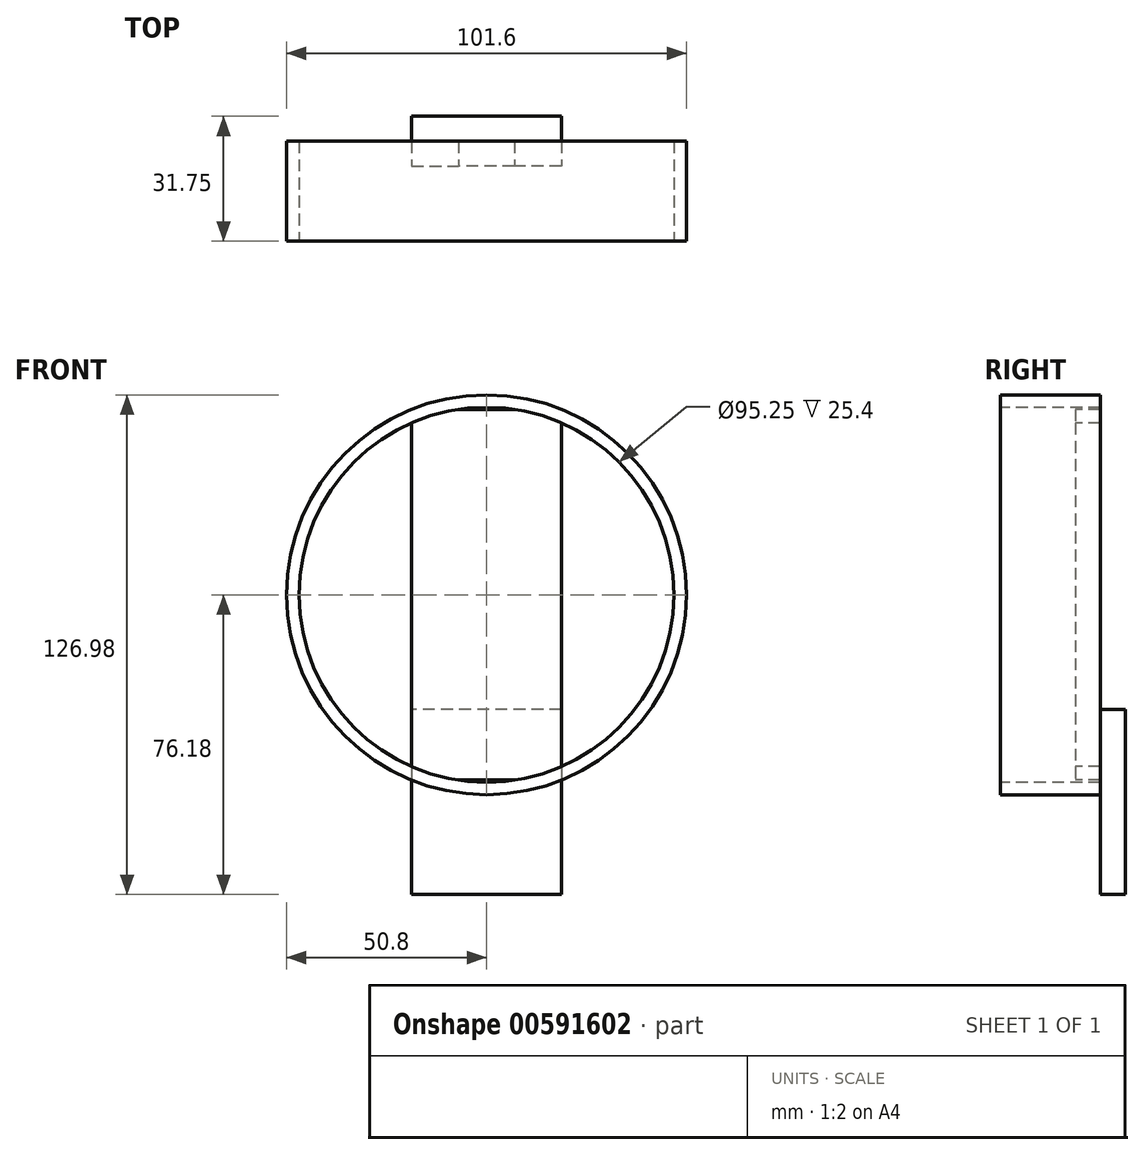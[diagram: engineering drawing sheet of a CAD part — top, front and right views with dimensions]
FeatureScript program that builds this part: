
annotation { "Feature Type Name" : "Feature", "Feature Type Description" : "" }
export const myFeature = defineFeature(function(context is Context, id is Id, definition is map)
    precondition{}
    {
        {
            var Q0;
            Q0=qCreatedBy(makeId("Front.planeOp"),FACE);
            var sketch = newSketch(context, id + "F0", { "sketchPlane" : qUnion([Q0])});
            skCircle(sketch, "E0", {"center": v(0, 0) * mm, "radius": 50.8 * mm});
            skSolve(sketch);
        }
        {
            var Q0;
            Q0 = qSketchRegion(id + "F0", true);
            extrude(context, id + "F1", {"entities" : qUnion([Q0]), "oppositeDirection" : true, "depth" : 25.4 * mm, "offsetDistance" : 25.4 * mm});
        }
        {
            var Q0;
            Q0=makeQuery(id+"F1.opExtrude","CAP_FACE",FACE,{"disambiguationData":[OSD([sQuery(id+"F0.wireOp",EDGE,"E0")])],"isStart":true});
            var sketch = newSketch(context, id + "F2", { "sketchPlane" : qUnion([Q0])});
            skCircle(sketch, "E1", {"center": v(0, 0) * mm, "radius": 47.63 * mm});
            skSolve(sketch);
        }
        {
            var Q0;
            Q0=makeQuery(id+"F2.imprint","IMPRINT",FACE,{"disambiguationData":[TD([[makeQuery(id+"F2.imprint","IMPRINT",EDGE,{"derivedFrom":sQuery(id+"F2.wireOp",EDGE,"E1")}),1.0]])]});
            extrude(context, id + "F3", {"entities" : qUnion([Q0]), "operationType" : NewBodyOperationType.REMOVE, "oppositeDirection" : true, "depth" : 25.4 * mm, "offsetDistance" : 25.4 * mm});
        }
        {
            var Q0;
            Q0=makeQuery(id+"F1.opExtrude","CAP_FACE",FACE,{"disambiguationData":[OSD([sQuery(id+"F0.wireOp",EDGE,"E0")])],"isStart":false});
            var sketch = newSketch(context, id + "F4", { "sketchPlane" : qUnion([Q0])});
            skLineSegment(sketch, "E2.bottom", {"start": v(-19.05, 47.1) * mm, "end": v(19.05, 47.1) * mm});
            skLineSegment(sketch, "E2.top", {"start": v(-19.05, -47.1) * mm, "end": v(19.05, -47.1) * mm});
            skLineSegment(sketch, "E2.left", {"start": v(-19.05, 47.1) * mm, "end": v(-19.05, -47.1) * mm});
            skLineSegment(sketch, "E2.right", {"start": v(19.05, 47.1) * mm, "end": v(19.05, -47.1) * mm});
            skSolve(sketch);
        }
        {
            var Q0;
            Q0 = qSketchRegion(id + "F4", true);
            extrude(context, id + "F5", {"entities" : qUnion([Q0]), "operationType" : NewBodyOperationType.ADD, "oppositeDirection" : true, "depth" : 6.35 * mm, "offsetDistance" : 25.4 * mm});
        }
        {
            var Q0;
            Q0=makeQuery(id+"F5.boolean.opBoolean","MERGE",FACE,{"derivedFrom":[makeQuery(id+"F1.opExtrude","CAP_FACE",FACE,{"disambiguationData":[OSD([sQuery(id+"F0.wireOp",EDGE,"E0")])],"isStart":false}),makeQuery(id+"F5.opExtrude","CAP_FACE",FACE,{"disambiguationData":[OSD([sQuery(id+"F4.wireOp",EDGE,"E2.bottom"),sQuery(id+"F4.wireOp",EDGE,"E2.top"),sQuery(id+"F4.wireOp",EDGE,"E2.left"),sQuery(id+"F4.wireOp",EDGE,"E2.right")])],"isStart":true})]});
            var sketch = newSketch(context, id + "F6", { "sketchPlane" : qUnion([Q0])});
            skLineSegment(sketch, "E3.bottom", {"start": v(-19.05, -29.2) * mm, "end": v(19.05, -29.2) * mm});
            skLineSegment(sketch, "E3.top", {"start": v(-19.05, -76.18) * mm, "end": v(19.05, -76.18) * mm});
            skLineSegment(sketch, "E3.left", {"start": v(-19.05, -29.2) * mm, "end": v(-19.05, -76.18) * mm});
            skLineSegment(sketch, "E3.right", {"start": v(19.05, -29.2) * mm, "end": v(19.05, -76.18) * mm});
            skSolve(sketch);
        }
        {
            var Q0;
            Q0 = qSketchRegion(id + "F6", true);
            extrude(context, id + "F7", {"entities" : qUnion([Q0]), "operationType" : NewBodyOperationType.ADD, "depth" : 6.35 * mm, "offsetDistance" : 25.4 * mm});
        }
    });
